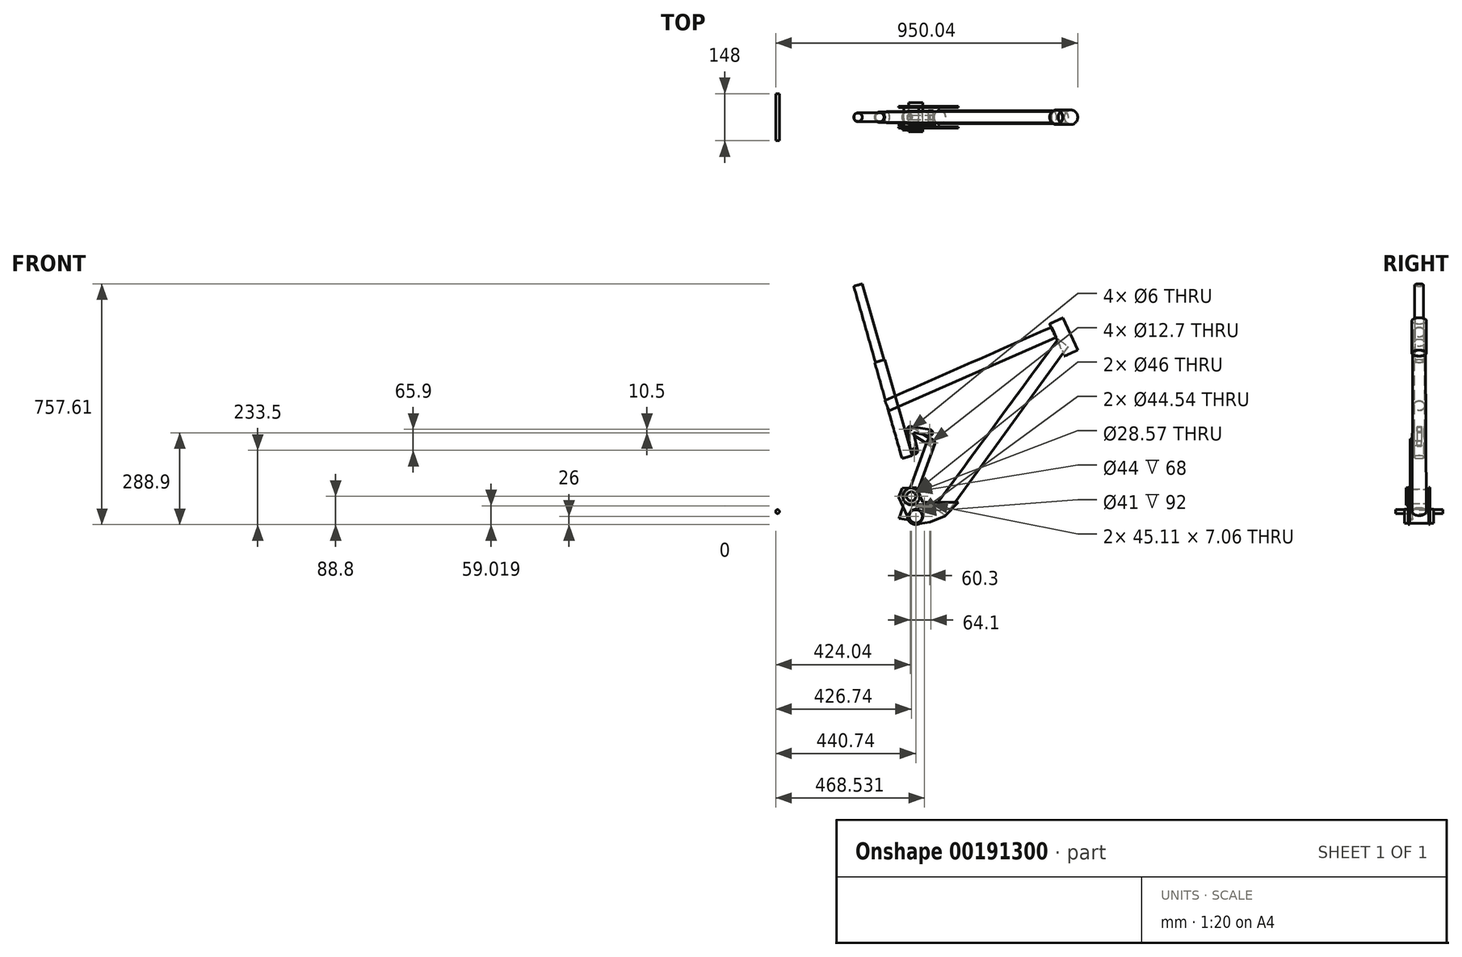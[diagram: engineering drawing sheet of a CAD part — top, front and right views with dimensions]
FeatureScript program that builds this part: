
annotation { "Feature Type Name" : "Feature", "Feature Type Description" : "" }
export const myFeature = defineFeature(function(context is Context, id is Id, definition is map)
    precondition{}
    {
        {
            var Q0;
            Q0=qCreatedBy(makeId("Front.planeOp"),FACE);
            var sketch = newSketch(context, id + "F0", { "sketchPlane" : qUnion([Q0])});
            skCircle(sketch, "E0", {"center": v(0, -15) * mm, "radius": 22.23 * mm});
            skCircle(sketch, "E1", {"center": v(-14, 47.8) * mm, "radius": 23 * mm});
            skLineSegment(sketch, "E2", {"start": v(0, -15) * mm, "end": v(488.28, 498.44) * mm});
            skLineSegment(sketch, "E3", {"start": v(488.28, 498.44) * mm, "end": v(442, 600) * mm});
            skLineSegment(sketch, "E4", {"start": v(442, 600) * mm, "end": v(-81.35, 361.5) * mm});
            skLineSegment(sketch, "E5", {"start": v(-81.35, 361.5) * mm, "end": v(-27.19, 171.47) * mm});
            skLineSegment(sketch, "E6", {"start": v(-434.74, 0) * mm, "end": v(715.44, 0) * mm, "construction": true});
            skLineSegment(sketch, "E7", {"start": v(715.44, 0) * mm, "end": v(442, 600) * mm, "construction": true});
            skLineSegment(sketch, "E8", {"start": v(442, 600) * mm, "end": v(0, 600) * mm, "construction": true});
            skLineSegment(sketch, "E9", {"start": v(-27.19, 171.47) * mm, "end": v(-181.44, 712.72) * mm});
            skLineSegment(sketch, "E10", {"start": v(0, 0) * mm, "end": v(0, -15) * mm});
            skLineSegment(sketch, "E11", {"start": v(0, -15) * mm, "end": v(-181.44, 712.72) * mm, "construction": true});
            skLineSegment(sketch, "E12", {"start": v(0, 600) * mm, "end": v(0, -15) * mm, "construction": true});
            skLineSegment(sketch, "E13", {"start": v(488.28, 498.44) * mm, "end": v(725.07, -21.15) * mm});
            skLineSegment(sketch, "E14", {"start": v(725.07, -21.15) * mm, "end": v(771.48, 0) * mm});
            skLineSegment(sketch, "E15", {"start": v(0, 0) * mm, "end": v(849.63, 0) * mm, "construction": true});
            skCircle(sketch, "E16", {"center": v(-434.74, 0) * mm, "radius": 365 * mm});
            skCircle(sketch, "E17", {"center": v(771.48, 0) * mm, "radius": 357 * mm});
            skLineSegment(sketch, "E18", {"start": v(-14, 47.8) * mm, "end": v(-14, -15) * mm, "construction": true});
            skLineSegment(sketch, "E19", {"start": v(0, -15) * mm, "end": v(60.1, -15) * mm, "construction": true});
            skLineSegment(sketch, "E20", {"start": v(0, -15) * mm, "end": v(0, 247.9) * mm, "construction": true});
            skLineSegment(sketch, "E21", {"start": v(0, 247.9) * mm, "end": v(43.6, 247.9) * mm, "construction": true});
            skLineSegment(sketch, "E22", {"start": v(0, 258.4) * mm, "end": v(-16.7, 258.4) * mm, "construction": true});
            skLineSegment(sketch, "E23", {"start": v(47.4, 215.6) * mm, "end": v(0, 215.6) * mm, "construction": true});
            skLineSegment(sketch, "E24", {"start": v(0, 63.8) * mm, "end": v(25.5, 63.8) * mm, "construction": true});
            skLineSegment(sketch, "E25", {"start": v(43.6, 247.9) * mm, "end": v(25.5, 63.8) * mm, "construction": true});
            skPoint(sketch, "E26", {"position": v(-5, 192.5) * mm});
            skLineSegment(sketch, "E27", {"start": v(-5, 192.5) * mm, "end": v(0, 192.5) * mm, "construction": true});
            skSolve(sketch);
        }
        {
            var Q0;
            Q0=qCreatedBy(makeId("Front.planeOp"),FACE);
            var sketch = newSketch(context, id + "F1", { "sketchPlane" : qUnion([Q0])});
            skLineSegment(sketch, "E28", {"start": v(462.02, 609.12) * mm, "end": v(508.3, 507.56) * mm});
            skLineSegment(sketch, "E29", {"start": v(508.3, 507.56) * mm, "end": v(509.3, 508.02) * mm});
            skLineSegment(sketch, "E30", {"start": v(509.3, 508.02) * mm, "end": v(463.02, 609.57) * mm});
            skLineSegment(sketch, "E31", {"start": v(463.02, 609.57) * mm, "end": v(462.02, 609.12) * mm});
            skLineSegment(sketch, "E32", {"start": v(462.02, 609.12) * mm, "end": v(442, 600) * mm, "construction": true});
            skLineSegment(sketch, "E33", {"start": v(508.3, 507.56) * mm, "end": v(488.28, 498.44) * mm, "construction": true});
            skSolve(sketch);
        }
        {
            var Q0;
            Q0=makeQuery(id+"F1.imprint","IMPRINT",FACE,{"disambiguationData":[TD([[makeQuery(id+"F1.imprint","IMPRINT",EDGE,{"derivedFrom":sQuery(id+"F1.wireOp",EDGE,"E28")}),1.0]])]});
            var Q1;
            Q1=sQuery(id+"F0.wireOp",EDGE,"E3");
            revolve(context, id + "F2", {"entities" : qUnion([Q0]), "axis" : qUnion([Q1]), "revolveType" : RevolveType.FULL});
        }
        {
            var Q0;
            Q0=qCreatedBy(makeId("Front.planeOp"),FACE);
            var sketch = newSketch(context, id + "F3", { "sketchPlane" : qUnion([Q0])});
            skLineSegment(sketch, "E34", {"start": v(75.66, 0) * mm, "end": v(449.57, 511.85) * mm, "construction": true});
            skLineSegment(sketch, "E35", {"start": v(93.5, -12.86) * mm, "end": v(479.56, 519.36) * mm});
            skLineSegment(sketch, "E36", {"start": v(479.56, 519.36) * mm, "end": v(478.87, 519.93) * mm});
            skLineSegment(sketch, "E37", {"start": v(478.87, 519.93) * mm, "end": v(92.78, -12.33) * mm});
            skLineSegment(sketch, "E38", {"start": v(92.78, -12.33) * mm, "end": v(93.5, -12.86) * mm});
            skLineSegment(sketch, "E39", {"start": v(463.13, 497.96) * mm, "end": v(467.27, 488.86) * mm, "construction": true});
            skLineSegment(sketch, "E40", {"start": v(93.5, -12.86) * mm, "end": v(75.66, 0) * mm, "construction": true});
            skSolve(sketch);
        }
        {
            var Q0;
            Q0=makeQuery(id+"F3.imprint","IMPRINT",FACE,{"disambiguationData":[TD([[makeQuery(id+"F3.imprint","IMPRINT",EDGE,{"derivedFrom":sQuery(id+"F3.wireOp",EDGE,"E35")}),1.0]])]});
            var Q1;
            Q1=sQuery(id+"F3.wireOp",EDGE,"E34");
            revolve(context, id + "F4", {"entities" : qUnion([Q0]), "axis" : qUnion([Q1]), "revolveType" : RevolveType.FULL});
        }
        {
            var Q0;
            Q0=qCreatedBy(makeId("Front.planeOp"),FACE);
            var sketch = newSketch(context, id + "F5", { "sketchPlane" : qUnion([Q0])});
            skCircle(sketch, "E41", {"center": v(0, -15) * mm, "radius": 22.27 * mm});
            skCircle(sketch, "E42", {"center": v(0, -15) * mm, "radius": 20.5 * mm});
            skSolve(sketch);
        }
        {
            var Q0;
            Q0=makeQuery(id+"F5.imprint","IMPRINT",FACE,{"disambiguationData":[TD([[makeQuery(id+"F5.imprint","IMPRINT",EDGE,{"derivedFrom":sQuery(id+"F5.wireOp",EDGE,"E41")}),1.0]])]});
            extrude(context, id + "F6", {"entities" : qUnion([Q0]), "endBound" : BoundingType.SYMMETRIC, "depth" : 92 * mm});
        }
        {
            var Q0;
            Q0=qCreatedBy(makeId("Front.planeOp"),FACE);
            var sketch = newSketch(context, id + "F7", { "sketchPlane" : qUnion([Q0])});
            skCircle(sketch, "E43", {"center": v(-14, 47.8) * mm, "radius": 23 * mm});
            skCircle(sketch, "E44", {"center": v(-14, 47.8) * mm, "radius": 22 * mm});
            skSolve(sketch);
        }
        {
            var Q0;
            Q0=makeQuery(id+"F7.imprint","IMPRINT",FACE,{"disambiguationData":[TD([[makeQuery(id+"F7.imprint","IMPRINT",EDGE,{"derivedFrom":sQuery(id+"F7.wireOp",EDGE,"E43")}),1.0]])]});
            extrude(context, id + "F8", {"entities" : qUnion([Q0]), "endBound" : BoundingType.SYMMETRIC, "depth" : 68 * mm});
        }
        {
            var Q0;
            Q0=makeQuery(id+"F8.opExtrude","CAP_FACE",FACE,{"disambiguationData":[OSD([sQuery(id+"F7.wireOp",EDGE,"E43"),sQuery(id+"F7.wireOp",EDGE,"E44")])],"isStart":false});
            var sketch = newSketch(context, id + "F9", { "sketchPlane" : qUnion([Q0])});
            skLineSegment(sketch, "E45", {"start": v(-26, -15.5) * mm, "end": v(-54.48, 45.5) * mm});
            skCircle(sketch, "E46", {"center": v(-14, 47.8) * mm, "radius": 27 * mm});
            skCircle(sketch, "E47", {"center": v(0, -15) * mm, "radius": 26 * mm});
            skCircle(sketch, "E48", {"center": v(-14, 47.8) * mm, "radius": 23 * mm});
            skCircle(sketch, "E49", {"center": v(0, -15) * mm, "radius": 22.27 * mm});
            skLineSegment(sketch, "E50", {"start": v(11.74, -38.2) * mm, "end": v(44.87, -32.67) * mm});
            skLineSegment(sketch, "E51", {"start": v(44.87, -32.67) * mm, "end": v(91.57, -14.22) * mm});
            skLineSegment(sketch, "E52", {"start": v(91.57, -14.22) * mm, "end": v(133.78, 29.47) * mm});
            skLineSegment(sketch, "E53", {"start": v(22.76, 28.78) * mm, "end": v(10.77, 58.54) * mm});
            skLineSegment(sketch, "E54", {"start": v(10.77, 58.54) * mm, "end": v(1.4, 76.37) * mm});
            skLineSegment(sketch, "E55", {"start": v(-54.48, 45.5) * mm, "end": v(-43.12, 73.43) * mm});
            skLineSegment(sketch, "E56", {"start": v(22.76, 28.78) * mm, "end": v(133.78, 29.47) * mm});
            skLineSegment(sketch, "E57", {"start": v(-43.12, 73.43) * mm, "end": v(1.4, 76.37) * mm});
            skCircle(sketch, "E58", {"center": v(25.5, 63.8) * mm, "radius": 4 * mm});
            skLineSegment(sketch, "E59.bottom", {"start": v(5.24, 21.55) * mm, "end": v(50.35, 21.55) * mm});
            skLineSegment(sketch, "E59.top", {"start": v(5.24, 14.49) * mm, "end": v(50.35, 14.49) * mm});
            skLineSegment(sketch, "E59.left", {"start": v(5.24, 21.55) * mm, "end": v(5.24, 14.49) * mm});
            skLineSegment(sketch, "E59.right", {"start": v(50.35, 21.55) * mm, "end": v(50.35, 14.49) * mm});
            skSolve(sketch);
        }
        {
            var Q0;
            Q0=makeQuery(id+"F9.imprint","IMPRINT",FACE,{"disambiguationData":[TD([[makeQuery(id+"F9.imprint","IMPRINT",EDGE,{"derivedFrom":sQuery(id+"F9.wireOp",EDGE,"E48")}),-1.0]])]});
            var Q1;
            {var subQ0=sQuery(id+"F9.wireOp",EDGE,"E47");var subQ1=sQuery(id+"F9.wireOp",EDGE,"E45");var subQ2=makeQuery(id+"F9.imprint","INTERSECT",VERTEX,{"derivedFrom":[subQ1,subQ0]});Q1=makeQuery(id+"F9.imprint","IMPRINT",FACE,{"disambiguationData":[TD([[makeQuery(id+"F9.imprint","IMPRINT",EDGE,{"disambiguationData":[TD([[subQ2,-1.0]])],"derivedFrom":subQ1}),-1.0]])]});}
            var Q2;
            Q2=makeQuery(id+"F9.imprint","IMPRINT",FACE,{"disambiguationData":[TD([[makeQuery(id+"F9.imprint","IMPRINT",EDGE,{"derivedFrom":sQuery(id+"F9.wireOp",EDGE,"E49")}),-1.0]])]});
            var Q3;
            {var subQ0=sQuery(id+"F9.wireOp",EDGE,"E54");Q3=makeQuery(id+"F9.imprint","IMPRINT",FACE,{"disambiguationData":[TD([[makeQuery(id+"F9.imprint","IMPRINT",EDGE,{"derivedFrom":subQ0}),1.0]])]});}
            extrude(context, id + "F10", {"entities" : qUnion([Q0, Q1, Q2, Q3]), "oppositeDirection" : true, "depth" : 4 * mm});
        }
        {
            var Q0;
            Q0=makeQuery(id+"F9.imprint","IMPRINT",FACE,{"disambiguationData":[TD([[makeQuery(id+"F9.imprint","IMPRINT",EDGE,{"derivedFrom":sQuery(id+"F9.wireOp",EDGE,"E48")}),-1.0]])]});
            var sketch = newSketch(context, id + "F11", { "sketchPlane" : qUnion([Q0])});
            skCircle(sketch, "E60", {"center": v(-14, 47.8) * mm, "radius": 27 * mm});
            skCircle(sketch, "E61", {"center": v(-14, 47.8) * mm, "radius": 14.29 * mm});
            skSolve(sketch);
        }
        {
            var Q0;
            Q0=makeQuery(id+"F11.imprint","IMPRINT",FACE,{"disambiguationData":[TD([[makeQuery(id+"F11.imprint","IMPRINT",EDGE,{"derivedFrom":makeQuery(id+"F9.imprint","IMPRINT",EDGE,{"derivedFrom":sQuery(id+"F9.wireOp",EDGE,"E48")})}),-1.0]])]});
            var Q1;
            Q1=makeQuery(id+"F11.imprint","IMPRINT",FACE,{"disambiguationData":[TD([[makeQuery(id+"F11.imprint","IMPRINT",EDGE,{"derivedFrom":sQuery(id+"F11.wireOp",EDGE,"E61")}),-1.0]])]});
            extrude(context, id + "F12", {"entities" : qUnion([Q0, Q1]), "depth" : 7 * mm});
        }
        {
            var Q0;
            Q0=qCreatedBy(makeId("Front.planeOp"),FACE);
            var sketch = newSketch(context, id + "F13", { "sketchPlane" : qUnion([Q0])});
            skCircle(sketch, "E62", {"center": v(-434.74, 0) * mm, "radius": 6 * mm});
            skSolve(sketch);
        }
        {
            var Q0;
            Q0=makeQuery(id+"F13.imprint","IMPRINT",FACE,{"disambiguationData":[TD([[makeQuery(id+"F13.imprint","IMPRINT",EDGE,{"derivedFrom":sQuery(id+"F13.wireOp",EDGE,"E62")}),1.0]])]});
            extrude(context, id + "F14", {"entities" : qUnion([Q0]), "endBound" : BoundingType.SYMMETRIC, "depth" : 148 * mm});
        }
        {
            var Q0;
            Q0=qCreatedBy(makeId("Front.planeOp"),FACE);
            var sketch = newSketch(context, id + "F15", { "sketchPlane" : qUnion([Q0])});
            skLineSegment(sketch, "E63", {"start": v(427.71, 580.34) * mm, "end": v(-97.54, 348.94) * mm});
            skLineSegment(sketch, "E64", {"start": v(-97.54, 348.94) * mm, "end": v(-97.18, 348.12) * mm});
            skLineSegment(sketch, "E65", {"start": v(427.71, 580.34) * mm, "end": v(428.08, 579.52) * mm});
            skLineSegment(sketch, "E66", {"start": v(428.08, 579.52) * mm, "end": v(-97.18, 348.12) * mm});
            skLineSegment(sketch, "E67", {"start": v(-90.48, 332.92) * mm, "end": v(434.77, 564.33) * mm, "construction": true});
            skLineSegment(sketch, "E68", {"start": v(-90.48, 332.92) * mm, "end": v(-97.54, 348.94) * mm, "construction": true});
            skLineSegment(sketch, "E69", {"start": v(434.77, 564.33) * mm, "end": v(427.71, 580.34) * mm, "construction": true});
            skSolve(sketch);
        }
        {
            var Q0;
            Q0=qSketchRegion(id+"F15",true);
            var Q1;
            Q1=sQuery(id+"F15.wireOp",EDGE,"E67");
            revolve(context, id + "F16", {"entities" : qUnion([Q0]), "axis" : qUnion([Q1]), "revolveType" : RevolveType.FULL});
        }
        {
            var Q0;
            Q0=qCreatedBy(makeId("Front.planeOp"),FACE);
            var sketch = newSketch(context, id + "F17", { "sketchPlane" : qUnion([Q0])});
            skLineSegment(sketch, "E70", {"start": v(-27.19, 171.47) * mm, "end": v(-113.27, 473.52) * mm, "construction": true});
            skLineSegment(sketch, "E71", {"start": v(-98.26, 477.77) * mm, "end": v(-12.19, 175.75) * mm});
            skLineSegment(sketch, "E72", {"start": v(-12.19, 175.75) * mm, "end": v(-11.32, 176) * mm});
            skLineSegment(sketch, "E73", {"start": v(-11.32, 176) * mm, "end": v(-97.4, 478.02) * mm});
            skLineSegment(sketch, "E74", {"start": v(-97.4, 478.02) * mm, "end": v(-98.26, 477.77) * mm});
            skLineSegment(sketch, "E75", {"start": v(-11.32, 176) * mm, "end": v(-27.19, 171.47) * mm, "construction": true});
            skLineSegment(sketch, "E76", {"start": v(-113.27, 473.52) * mm, "end": v(-97.4, 478.02) * mm, "construction": true});
            skSolve(sketch);
        }
        {
            var Q0;
            Q0=makeQuery(id+"F17.imprint","IMPRINT",FACE,{"disambiguationData":[TD([[makeQuery(id+"F17.imprint","IMPRINT",EDGE,{"derivedFrom":sQuery(id+"F17.wireOp",EDGE,"E71")}),1.0]])]});
            var Q1;
            Q1=sQuery(id+"F0.wireOp",EDGE,"E9");
            revolve(context, id + "F18", {"entities" : qUnion([Q0]), "axis" : qUnion([Q1]), "revolveType" : RevolveType.FULL});
        }
        {
            var Q0;
            Q0=qCreatedBy(makeId("Front.planeOp"),FACE);
            var sketch = newSketch(context, id + "F19", { "sketchPlane" : qUnion([Q0])});
            skLineSegment(sketch, "E77", {"start": v(-181.44, 712.72) * mm, "end": v(-113.26, 473.5) * mm, "construction": true});
            skLineSegment(sketch, "E78", {"start": v(-113.26, 473.5) * mm, "end": v(-100.48, 477.14) * mm, "construction": true});
            skLineSegment(sketch, "E79", {"start": v(-100.48, 477.14) * mm, "end": v(-168.66, 716.36) * mm});
            skLineSegment(sketch, "E80", {"start": v(-168.66, 716.36) * mm, "end": v(-181.44, 712.72) * mm, "construction": true});
            skLineSegment(sketch, "E81", {"start": v(-167.8, 716.61) * mm, "end": v(-168.66, 716.36) * mm, "construction": true});
            skLineSegment(sketch, "E82", {"start": v(-167.8, 716.61) * mm, "end": v(-99.62, 477.39) * mm});
            skLineSegment(sketch, "E83", {"start": v(-100.48, 477.14) * mm, "end": v(-99.62, 477.39) * mm});
            skLineSegment(sketch, "E84", {"start": v(-168.66, 716.36) * mm, "end": v(-167.8, 716.61) * mm});
            skSolve(sketch);
        }
        {
            var Q0;
            Q0=makeQuery(id+"F19.imprint","IMPRINT",FACE,{"disambiguationData":[TD([[makeQuery(id+"F19.imprint","IMPRINT",EDGE,{"derivedFrom":sQuery(id+"F19.wireOp",EDGE,"E79")}),-1.0]])]});
            var Q1;
            Q1=sQuery(id+"F0.wireOp",EDGE,"E9");
            revolve(context, id + "F20", {"entities" : qUnion([Q0]), "axis" : qUnion([Q1]), "revolveType" : RevolveType.FULL});
        }
        {
            var Q0;
            Q0=qCreatedBy(makeId("Front.planeOp"),FACE);
            var sketch = newSketch(context, id + "F21", { "sketchPlane" : qUnion([Q0])});
            skCircle(sketch, "E85", {"center": v(47.4, 215.6) * mm, "radius": 7.5 * mm});
            skSolve(sketch);
        }
        {
            var Q0;
            Q0=makeQuery(id+"F21.imprint","IMPRINT",FACE,{"disambiguationData":[TD([[makeQuery(id+"F21.imprint","IMPRINT",EDGE,{"derivedFrom":sQuery(id+"F21.wireOp",EDGE,"E85")}),1.0]])]});
            extrude(context, id + "F22", {"entities" : qUnion([Q0]), "endBound" : BoundingType.SYMMETRIC, "depth" : 40 * mm});
        }
        {
            var Q0;
            Q0=qCreatedBy(makeId("Front.planeOp"),FACE);
            cPlane(context, id + "F23", {"entities" : qUnion([Q0]), "cplaneType" : CPlaneType.OFFSET, "offset" : 15 * mm, "width" : 150 * mm, "height" : 150 * mm});
        }
        {
            var Q0;
            Q0=qCreatedBy(id+"F23.planeOp",FACE);
            var sketch = newSketch(context, id + "F24", { "sketchPlane" : qUnion([Q0])});
            skCircle(sketch, "E86", {"center": v(-16.7, 258.4) * mm, "radius": 3 * mm});
            skCircle(sketch, "E87", {"center": v(47.4, 215.6) * mm, "radius": 6.35 * mm});
            skArc(sketch, "E88", {"start": v(-15.52, 268.33) * mm, "mid": v(-23.95, 265.29) * mm, "end": v(-26.56, 256.72) * mm});
            skLineSegment(sketch, "E89", {"start": v(-26.56, 256.72) * mm, "end": v(-14.22, 184.34) * mm});
            skCircle(sketch, "E90", {"center": v(43.6, 247.9) * mm, "radius": 3 * mm});
            skCircle(sketch, "E91", {"center": v(-5, 192.5) * mm, "radius": 6.35 * mm});
            skArc(sketch, "E92", {"start": v(39.77, 238.66) * mm, "mid": v(53.24, 245.22) * mm, "end": v(45.08, 257.79) * mm});
            skLineSegment(sketch, "E93", {"start": v(-15.52, 268.33) * mm, "end": v(45.08, 257.79) * mm});
            skArc(sketch, "E94", {"start": v(-14.22, 184.34) * mm, "mid": v(-3.03, 180.35) * mm, "end": v(6.32, 187.68) * mm});
            skLineSegment(sketch, "E95", {"start": v(6.32, 187.68) * mm, "end": v(-7.57, 249.15) * mm});
            skLineSegment(sketch, "E96", {"start": v(-7.57, 249.15) * mm, "end": v(39.77, 238.66) * mm});
            skSolve(sketch);
        }
        {
            var Q0;
            Q0=makeQuery(id+"F24.imprint","IMPRINT",FACE,{"disambiguationData":[TD([[makeQuery(id+"F24.imprint","IMPRINT",EDGE,{"derivedFrom":sQuery(id+"F24.wireOp",EDGE,"E86")}),-1.0]])]});
            extrude(context, id + "F25", {"entities" : qUnion([Q0]), "depth" : 4 * mm});
        }
        {
            var Q0;
            Q0=makeQuery(id+"F10.opExtrude","SWEPT_BODY",BODY,{"disambiguationData":[OSD([sQuery(id+"F9.wireOp",EDGE,"E45"),sQuery(id+"F9.wireOp",EDGE,"E46"),sQuery(id+"F9.wireOp",EDGE,"E47"),sQuery(id+"F9.wireOp",EDGE,"E48"),sQuery(id+"F9.wireOp",EDGE,"E49"),sQuery(id+"F9.wireOp",EDGE,"E50"),sQuery(id+"F9.wireOp",EDGE,"E51"),sQuery(id+"F9.wireOp",EDGE,"E52"),sQuery(id+"F9.wireOp",EDGE,"E53"),sQuery(id+"F9.wireOp",EDGE,"E55"),sQuery(id+"F9.wireOp",EDGE,"E56"),sQuery(id+"F9.wireOp",EDGE,"FK5K02xT-Tyjw-d1qf-akf6-uhemaVaazLAm"),sQuery(id+"F9.wireOp",EDGE,"mm2pKiwS-SVnP-zvIU-L5Du-A2j7p1U8S5B2"),sQuery(id+"F9.wireOp",EDGE,"IZCLW8zM-GbKn-ctCs-2ocb-lbeokmNvXhk3"),sQuery(id+"F9.wireOp",EDGE,"xYsf3Ban-L5P9-4PwF-GR1m-Uv2y4zeUiWQ5"),sQuery(id+"F9.wireOp",EDGE,"yQkTHGf5-sRyh-42L4-Ud2E-ts9FopTQnuyI"),sQuery(id+"F9.wireOp",EDGE,"t0aHAust-p0Rk-zyfR-vzEr-3oL8Lvwd0bzb"),sQuery(id+"F9.wireOp",EDGE,"Ufxdm7CI-QsJz-9KF8-LKNm-jGi75a7C4uIL"),sQuery(id+"F9.wireOp",EDGE,"ZnK2q6qZ-2Q7Z-vcdy-yBDD-ScY7AwOiJMqo"),sQuery(id+"F9.wireOp",EDGE,"Gc7Wburp-0UPy-ylzU-ry04-YMOsavYO6OQT"),sQuery(id+"F9.wireOp",EDGE,"cUvrFAy7-kfZD-SUgz-PhUw-DuEA4dqAJlpC"),sQuery(id+"F9.wireOp",EDGE,"pkUo2EjT-BdgE-IHWr-ZNv9-eBEOamu1rOXd"),sQuery(id+"F9.wireOp",EDGE,"YDDUzq19-sVF8-QGLi-mOwB-5G3ZNUy8fJTz")])]});
            var Q1;
            Q1=qCreatedBy(makeId("Front.planeOp"),FACE);
            mirror(context, id + "F26", {"entities" : qUnion([Q0]), "mirrorPlane" : qUnion([Q1])});
        }
        {
            var Q0;
            Q0=makeQuery(id+"F25.opExtrude","SWEPT_BODY",BODY,{"disambiguationData":[OSD([sQuery(id+"F24.wireOp",EDGE,"E86"),sQuery(id+"F24.wireOp",EDGE,"E87"),sQuery(id+"F24.wireOp",EDGE,"dAnCmmoZ-466u-qX6o-hDcC-m3oDPRMVMXJO"),sQuery(id+"F24.wireOp",EDGE,"aSv8fLUU-wUDJ-uzsc-UppV-udqLk2aLprjb"),sQuery(id+"F24.wireOp",EDGE,"Yv7OH4Xu-fMxE-rXm1-8sic-hcBzgtiXKYZb"),sQuery(id+"F24.wireOp",EDGE,"tyVKKrEt-jyp4-oobT-BweY-p1mvCkoPBQRs")])]});
            var Q1;
            Q1=qCreatedBy(makeId("Front.planeOp"),FACE);
            mirror(context, id + "F27", {"operationType" : NewBodyOperationType.ADD, "entities" : qUnion([Q0]), "mirrorPlane" : qUnion([Q1])});
        }
        {
            var Q0;
            Q0=makeQuery(id+"F22.opExtrude","CAP_FACE",FACE,{"disambiguationData":[OSD([sQuery(id+"F21.wireOp",EDGE,"E85")])],"isStart":false});
            cPlane(context, id + "F28", {"entities" : qUnion([Q0]), "cplaneType" : CPlaneType.OFFSET, "offset" : 0 * mm, "width" : 150 * mm, "height" : 150 * mm});
        }
        {
            var Q0;
            Q0=qCreatedBy(id+"F28.planeOp",FACE);
            var sketch = newSketch(context, id + "F29", { "sketchPlane" : qUnion([Q0])});
            skLineSegment(sketch, "E97", {"start": v(-27.37, -25.52) * mm, "end": v(-52.9, -21.45) * mm});
            skLineSegment(sketch, "E98", {"start": v(-52.9, -21.45) * mm, "end": v(36.62, 222.72) * mm});
            skLineSegment(sketch, "E99", {"start": v(60.03, 212.86) * mm, "end": v(-27.37, -25.52) * mm});
            skArc(sketch, "E100", {"start": v(60.03, 212.86) * mm, "mid": v(52.42, 227.5) * mm, "end": v(36.62, 222.72) * mm});
            skCircle(sketch, "E101", {"center": v(-14, 47.8) * mm, "radius": 23.2 * mm});
            skLineSegment(sketch, "E102", {"start": v(-27.51, 47.8) * mm, "end": v(-0.49, 47.8) * mm, "construction": true});
            skSolve(sketch);
        }
        {
            var Q0;
            {var subQ0=sQuery(id+"F29.wireOp",EDGE,"E100");Q0=makeQuery(id+"F29.imprint","IMPRINT",FACE,{"disambiguationData":[TD([[makeQuery(id+"F29.imprint","IMPRINT",EDGE,{"derivedFrom":subQ0}),1.0]])]});}
            var Q1;
            {var subQ0=sQuery(id+"F29.wireOp",EDGE,"E97");Q1=makeQuery(id+"F29.imprint","IMPRINT",FACE,{"disambiguationData":[TD([[makeQuery(id+"F29.imprint","IMPRINT",EDGE,{"derivedFrom":subQ0}),-1.0]])]});}
            extrude(context, id + "F30", {"entities" : qUnion([Q0, Q1]), "depth" : 8 * mm});
        }
        {
            var Q0;
            Q0=qCreatedBy(makeId("Front.planeOp"),FACE);
            var sketch = newSketch(context, id + "F31", { "sketchPlane" : qUnion([Q0])});
            skCircle(sketch, "E103", {"center": v(-16.7, 258.4) * mm, "radius": 10 * mm});
            skCircle(sketch, "E104", {"center": v(47.4, 215.6) * mm, "radius": 10 * mm});
            skLineSegment(sketch, "E105", {"start": v(-14.27, 268.1) * mm, "end": v(52.9, 223.96) * mm});
            skLineSegment(sketch, "E106", {"start": v(-17.64, 248.44) * mm, "end": v(46.84, 205.62) * mm});
            skCircle(sketch, "E107", {"center": v(-16.7, 258.4) * mm, "radius": 6.35 * mm});
            skCircle(sketch, "E108", {"center": v(47.4, 215.6) * mm, "radius": 6.35 * mm});
            skSolve(sketch);
        }
        {
            var Q0;
            {var subQ0=sQuery(id+"F31.wireOp",EDGE,"E106");var subQ1=sQuery(id+"F31.wireOp",EDGE,"E103");var subQ2=makeQuery(id+"F31.imprint","INTERSECT",VERTEX,{"derivedFrom":[subQ1,subQ0]});Q0=makeQuery(id+"F31.imprint","IMPRINT",FACE,{"disambiguationData":[TD([[makeQuery(id+"F31.imprint","IMPRINT",EDGE,{"disambiguationData":[TD([[subQ2,-1.0]])],"derivedFrom":subQ1}),-1.0]])]});}
            var Q1;
            Q1=makeQuery(id+"F31.imprint","IMPRINT",FACE,{"disambiguationData":[TD([[makeQuery(id+"F31.imprint","IMPRINT",EDGE,{"derivedFrom":sQuery(id+"F31.wireOp",EDGE,"E107")}),-1.0]])]});
            var Q2;
            Q2=makeQuery(id+"F31.imprint","IMPRINT",FACE,{"disambiguationData":[TD([[makeQuery(id+"F31.imprint","IMPRINT",EDGE,{"derivedFrom":sQuery(id+"F31.wireOp",EDGE,"E108")}),-1.0]])]});
            extrude(context, id + "F32", {"entities" : qUnion([Q0, Q1, Q2]), "endBound" : BoundingType.SYMMETRIC, "depth" : 14 * mm});
        }
    });
